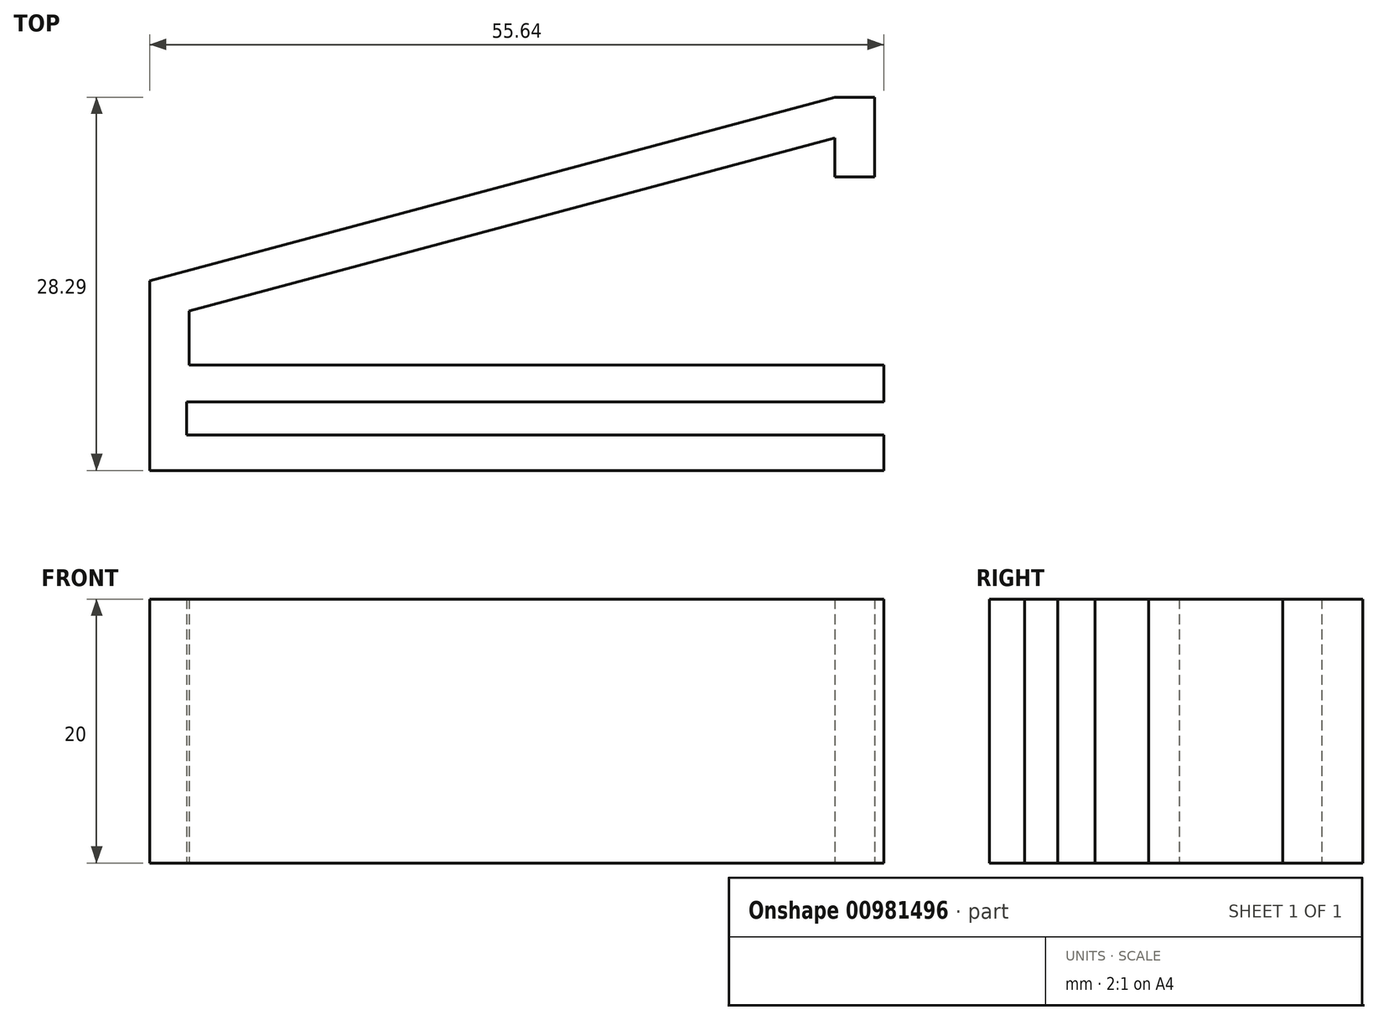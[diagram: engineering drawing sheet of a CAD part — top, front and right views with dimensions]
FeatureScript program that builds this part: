
annotation { "Feature Type Name" : "Feature", "Feature Type Description" : "" }
export const myFeature = defineFeature(function(context is Context, id is Id, definition is map)
    precondition{}
    {
        {
            var Q0;
            Q0=qCreatedBy(makeId("Front.planeOp"),FACE);
            var sketch = newSketch(context, id + "F0", { "sketchPlane" : qUnion([Q0])});
            skLineSegment(sketch, "E0.bottom", {"start": v(-27.82, 10) * mm, "end": v(27.82, 10) * mm});
            skLineSegment(sketch, "E0.top", {"start": v(-27.82, -10) * mm, "end": v(27.82, -10) * mm});
            skLineSegment(sketch, "E0.left", {"start": v(-27.82, 10) * mm, "end": v(-27.82, -10) * mm});
            skLineSegment(sketch, "E0.right", {"start": v(27.82, 10) * mm, "end": v(27.82, -10) * mm});
            skLineSegment(sketch, "E1", {"start": v(27.82, 0) * mm, "end": v(-78.3, 0) * mm, "construction": true});
            skPoint(sketch, "E2", {"position": v(-27.82, 0) * mm});
            skLineSegment(sketch, "E3", {"start": v(-61.14, 0) * mm, "end": v(109.13, 0) * mm, "construction": true});
            skLineSegment(sketch, "E4", {"start": v(0, -83.7) * mm, "end": v(0, 95.89) * mm, "construction": true});
            skPoint(sketch, "E4.startSnap0", {"position": v(0, -10) * mm});
            skPoint(sketch, "E5", {"position": v(0, 0) * mm});
            skSolve(sketch);
        }
        {
            var Q0;
            Q0=makeQuery(id+"F0.imprint","IMPRINT",FACE,{"disambiguationData":[TD([[makeQuery(id+"F0.imprint","IMPRINT",EDGE,{"derivedFrom":sQuery(id+"F0.wireOp",EDGE,"E0.bottom")}),-1.0]])]});
            extrude(context, id + "F1", {"entities" : qUnion([Q0]), "oppositeDirection" : true, "depth" : 8 * mm, "offsetDistance" : 25 * mm});
        }
        {
            var Q0;
            Q0=qCreatedBy(makeId("Right.planeOp"),FACE);
            var sketch = newSketch(context, id + "F2", { "sketchPlane" : qUnion([Q0])});
            skLineSegment(sketch, "E6", {"start": v(3.93, 51.3) * mm, "end": v(3.93, -48.28) * mm, "construction": true});
            skLineSegment(sketch, "E7.bottom", {"start": v(2.68, 20) * mm, "end": v(5.18, 20) * mm});
            skLineSegment(sketch, "E7.top", {"start": v(2.68, -20) * mm, "end": v(5.18, -20) * mm});
            skLineSegment(sketch, "E7.left", {"start": v(2.68, 20) * mm, "end": v(2.68, -20) * mm});
            skLineSegment(sketch, "E7.right", {"start": v(5.18, 20) * mm, "end": v(5.18, -20) * mm});
            skPoint(sketch, "E8", {"position": v(3.93, 0) * mm});
            skPoint(sketch, "E9", {"position": v(5.18, 0) * mm});
            skLineSegment(sketch, "E10", {"start": v(11.77, 0) * mm, "end": v(-5.55, 0) * mm, "construction": true});
            skPoint(sketch, "E11.positionSnap0", {"position": v(3.93, -20) * mm});
            skSolve(sketch);
        }
        {
            var Q0;
            Q0=makeQuery(id+"FBMLdxI11pTwmpj_1.opExtractSurface","COPY",FACE,{"derivedFrom":makeQuery(id+"F2.imprint","IMPRINT",FACE,{"disambiguationData":[TD([[makeQuery(id+"F2.imprint","IMPRINT",EDGE,{"derivedFrom":sQuery(id+"F2.wireOp",EDGE,"E7.bottom")}),-1.0]])]})});
            var Q1;
            Q1=makeQuery(id+"F2.imprint","IMPRINT",FACE,{"disambiguationData":[TD([[makeQuery(id+"F2.imprint","IMPRINT",EDGE,{"derivedFrom":sQuery(id+"F2.wireOp",EDGE,"E7.bottom")}),-1.0]])]});
            extrude(context, id + "F3", {"entities" : qUnion([Q0, Q1]), "operationType" : NewBodyOperationType.REMOVE, "endBound" : BoundingType.THROUGH_ALL, "depth" : 25 * mm, "offsetDistance" : 25 * mm, "hasSecondDirection" : true, "secondDirectionOppositeDirection" : true, "secondDirectionDepth" : 25 * mm});
        }
        {
            var Q0;
            Q0=qCreatedBy(makeId("Top.planeOp"),FACE);
            var sketch = newSketch(context, id + "F4", { "sketchPlane" : qUnion([Q0])});
            skLineSegment(sketch, "E12", {"start": v(-27.82, 14.37) * mm, "end": v(24.11, 28.29) * mm});
            skLineSegment(sketch, "E13", {"start": v(24.11, 28.29) * mm, "end": v(27.11, 28.28) * mm});
            skLineSegment(sketch, "E14", {"start": v(24.11, 25.18) * mm, "end": v(-24.82, 12.07) * mm});
            skLineSegment(sketch, "E15", {"start": v(-24.82, 12.07) * mm, "end": v(-24.82, 8) * mm});
            skLineSegment(sketch, "E16.0", {"start": v(-27.82, 8) * mm, "end": v(-27.82, 0) * mm, "construction": true});
            skLineSegment(sketch, "E17.0", {"start": v(-27.82, 8) * mm, "end": v(27.82, 8) * mm, "construction": true});
            skLineSegment(sketch, "E18", {"start": v(-27.82, 8) * mm, "end": v(-27.82, 14.37) * mm});
            skLineSegment(sketch, "E19", {"start": v(-24.82, 8) * mm, "end": v(-27.82, 8) * mm});
            skLineSegment(sketch, "E20", {"start": v(24.11, 28.29) * mm, "end": v(24.11, 22.23) * mm});
            skLineSegment(sketch, "E21", {"start": v(24.11, 22.23) * mm, "end": v(27.11, 22.23) * mm});
            skLineSegment(sketch, "E22", {"start": v(27.11, 22.23) * mm, "end": v(27.11, 28.28) * mm});
            skSolve(sketch);
        }
        {
            var Q0;
            Q0=qSketchRegion(id+"F4",true);
            extrude(context, id + "F5", {"entities" : qUnion([Q0]), "operationType" : NewBodyOperationType.ADD, "endBound" : BoundingType.SYMMETRIC, "depth" : 20 * mm, "offsetDistance" : 25 * mm});
        }
    });
